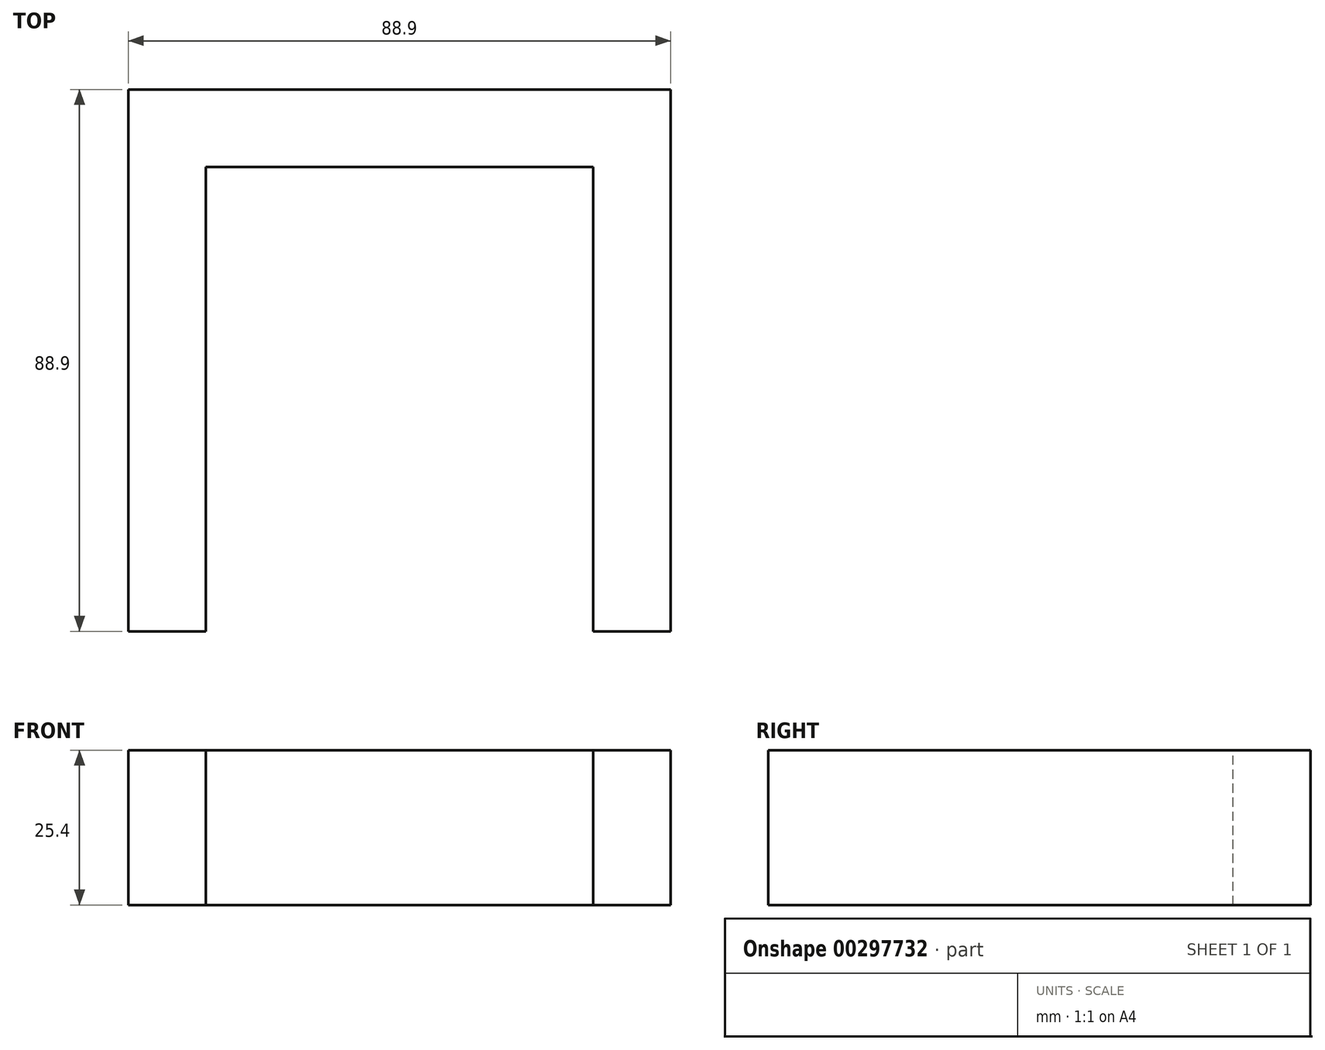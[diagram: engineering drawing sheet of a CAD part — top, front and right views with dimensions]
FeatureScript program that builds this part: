
annotation { "Feature Type Name" : "Feature", "Feature Type Description" : "" }
export const myFeature = defineFeature(function(context is Context, id is Id, definition is map)
    precondition{}
    {
        {
            var Q0;
            Q0=qCreatedBy(makeId("Top.planeOp"),FACE);
            var sketch = newSketch(context, id + "F0", { "sketchPlane" : qUnion([Q0])});
            skLineSegment(sketch, "E0.bottom", {"start": v(44.45, -44.45) * mm, "end": v(-44.45, -44.45) * mm});
            skLineSegment(sketch, "E0.top", {"start": v(44.45, 44.45) * mm, "end": v(-44.45, 44.45) * mm});
            skLineSegment(sketch, "E0.left", {"start": v(44.45, -44.45) * mm, "end": v(44.45, 44.45) * mm});
            skLineSegment(sketch, "E0.right", {"start": v(-44.45, -44.45) * mm, "end": v(-44.45, 44.45) * mm});
            skPoint(sketch, "E0.middle", {"position": v(0, 0) * mm});
            skSolve(sketch);
        }
        {
            var Q0;
            Q0 = qSketchRegion(id + "F0", true);
            extrude(context, id + "F1", {"entities" : qUnion([Q0]), "endBound" : BoundingType.SYMMETRIC, "depth" : 25.4 * mm});
        }
        {
            var Q0;
            Q0=makeQuery(id+"F1.opExtrude","CAP_FACE",FACE,{"disambiguationData":[OSD([sQuery(id+"F0.wireOp",EDGE,"E0.bottom"),sQuery(id+"F0.wireOp",EDGE,"E0.top"),sQuery(id+"F0.wireOp",EDGE,"E0.left"),sQuery(id+"F0.wireOp",EDGE,"E0.right")])],"isStart":false});
            var sketch = newSketch(context, id + "F2", { "sketchPlane" : qUnion([Q0])});
            skLineSegment(sketch, "E1.bottom", {"start": v(-31.75, -44.45) * mm, "end": v(31.75, -44.45) * mm});
            skLineSegment(sketch, "E1.top", {"start": v(-31.75, 31.75) * mm, "end": v(31.75, 31.75) * mm});
            skLineSegment(sketch, "E1.left", {"start": v(-31.75, -44.45) * mm, "end": v(-31.75, 31.75) * mm});
            skLineSegment(sketch, "E1.right", {"start": v(31.75, -44.45) * mm, "end": v(31.75, 31.75) * mm});
            skLineSegment(sketch, "E2", {"start": v(0, 0) * mm, "end": v(0, -68.69) * mm, "construction": true});
            skSolve(sketch);
        }
        {
            var Q0;
            Q0 = qSketchRegion(id + "F2", true);
            extrude(context, id + "F3", {"entities" : qUnion([Q0]), "operationType" : NewBodyOperationType.REMOVE, "endBound" : BoundingType.THROUGH_ALL, "oppositeDirection" : true, "depth" : 25.4 * mm});
        }
    });
